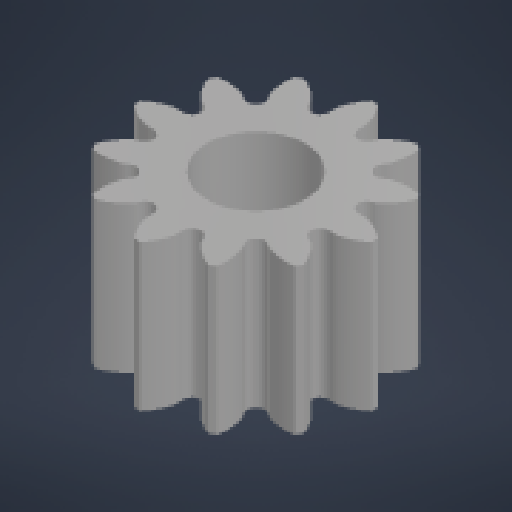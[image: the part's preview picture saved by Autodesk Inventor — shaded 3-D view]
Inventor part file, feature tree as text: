
AUTODESK INVENTOR PART (.ipt)
format: ipt  version: 2024 (Build 280153000, 153)  size: 428,032 bytes
history: native  units: mm
features: extrude x2, sketch x2, projected_geometry x2, other x1, imported_body x1
ambient origin geometry x8: Origin, YZ Plane, XZ Plane, XY Plane, X Axis, Y Axis, Z Axis, Center Point
bodies: Body1 (feature_tree)
feature tree (8):
  other  "Твердое тело1"
  extrude  "Выдавливание1"  Depth=3.0mm TaperAngle=0.0deg
  extrude  "Выдавливание2"  Depth=3.0mm TaperAngle=0.0deg
  sketch  "Эскиз1"
  projected_geometry  "Спроецированная петля1"
  sketch  "Эскиз2"
  projected_geometry  "Спроецированная петля2"
  imported_body  "БазТело1"
